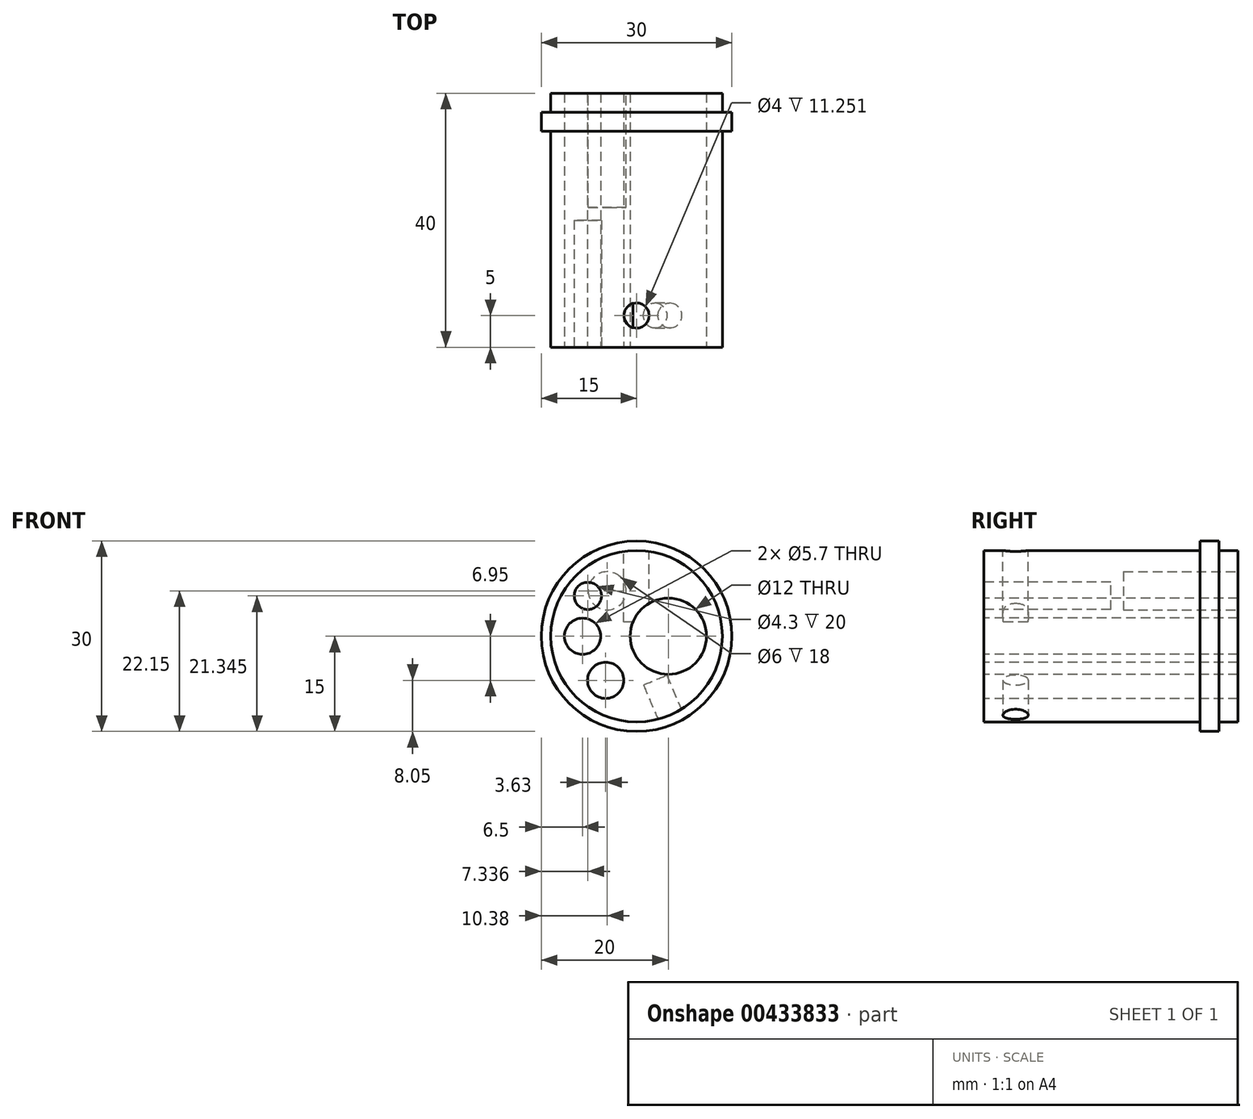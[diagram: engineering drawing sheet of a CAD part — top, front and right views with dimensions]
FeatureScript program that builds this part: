
annotation { "Feature Type Name" : "Feature", "Feature Type Description" : "" }
export const myFeature = defineFeature(function(context is Context, id is Id, definition is map)
    precondition{}
    {
        {
            var Q0;
            Q0=qCreatedBy(makeId("Front.planeOp"),FACE);
            var sketch = newSketch(context, id + "F0", { "sketchPlane" : qUnion([Q0])});
            skCircle(sketch, "E0", {"center": v(0, 0) * mm, "radius": 15 * mm});
            skSolve(sketch);
        }
        {
            var Q0;
            Q0 = qSketchRegion(id + "F0", true);
            extrude(context, id + "F1", {"entities" : qUnion([Q0]), "oppositeDirection" : true, "depth" : 40 * mm});
        }
        {
            var Q0;
            Q0=makeQuery(id+"F1.opExtrude","CAP_FACE",FACE,{"disambiguationData":[OSD([sQuery(id+"F0.wireOp",EDGE,"E0")])],"isStart":true});
            var sketch = newSketch(context, id + "F2", { "sketchPlane" : qUnion([Q0])});
            skCircle(sketch, "E1", {"center": v(0, 0) * mm, "radius": 25.45 * mm});
            skCircle(sketch, "E2", {"center": v(0, 0) * mm, "radius": 13.5 * mm});
            skSolve(sketch);
        }
        {
            var Q0;
            Q0 = qSketchRegion(id + "F2", true);
            extrude(context, id + "F3", {"entities" : qUnion([Q0]), "operationType" : NewBodyOperationType.REMOVE, "oppositeDirection" : true, "depth" : 34 * mm});
        }
        {
            var Q0;
            Q0=makeQuery(id+"F1.opExtrude","CAP_FACE",FACE,{"disambiguationData":[OSD([sQuery(id+"F0.wireOp",EDGE,"E0")])],"isStart":false});
            var sketch = newSketch(context, id + "F4", { "sketchPlane" : qUnion([Q0])});
            skCircle(sketch, "E3", {"center": v(0, 0) * mm, "radius": 18.73 * mm});
            skCircle(sketch, "E4", {"center": v(0, 0) * mm, "radius": 13.5 * mm});
            skSolve(sketch);
        }
        {
            var Q0;
            Q0 = qSketchRegion(id + "F4", true);
            extrude(context, id + "F5", {"entities" : qUnion([Q0]), "operationType" : NewBodyOperationType.REMOVE, "oppositeDirection" : true, "depth" : 3 * mm});
        }
        {
            var Q0;
            Q0=makeQuery(id+"F1.opExtrude","CAP_FACE",FACE,{"disambiguationData":[OSD([sQuery(id+"F0.wireOp",EDGE,"E0")])],"isStart":true});
            var sketch = newSketch(context, id + "F6", { "sketchPlane" : qUnion([Q0])});
            skCircle(sketch, "E5", {"center": v(5, 0) * mm, "radius": 6 * mm});
            skSolve(sketch);
        }
        {
            var Q0;
            Q0 = qSketchRegion(id + "F6", true);
            extrude(context, id + "F7", {"entities" : qUnion([Q0]), "operationType" : NewBodyOperationType.REMOVE, "endBound" : BoundingType.THROUGH_ALL, "oppositeDirection" : true, "depth" : 25 * mm});
        }
        {
            var Q0;
            Q0=makeQuery(id+"F1.opExtrude","CAP_FACE",FACE,{"disambiguationData":[OSD([sQuery(id+"F0.wireOp",EDGE,"E0")])],"isStart":true});
            var sketch = newSketch(context, id + "F8", { "sketchPlane" : qUnion([Q0])});
            skCircle(sketch, "E6", {"center": v(-4.87, -6.95) * mm, "radius": 2.85 * mm});
            skSolve(sketch);
        }
        {
            var Q0;
            Q0 = qSketchRegion(id + "F8", true);
            extrude(context, id + "F9", {"entities" : qUnion([Q0]), "operationType" : NewBodyOperationType.REMOVE, "endBound" : BoundingType.THROUGH_ALL, "oppositeDirection" : true, "depth" : 25 * mm});
        }
        {
            var Q0;
            Q0=makeQuery(id+"F1.opExtrude","CAP_FACE",FACE,{"disambiguationData":[OSD([sQuery(id+"F0.wireOp",EDGE,"E0")])],"isStart":true});
            var sketch = newSketch(context, id + "F10", { "sketchPlane" : qUnion([Q0])});
            skCircle(sketch, "E7", {"center": v(-8.5, 0) * mm, "radius": 2.85 * mm});
            skPoint(sketch, "E8", {"position": v(-4.87, -6.95) * mm});
            skSolve(sketch);
        }
        {
            var Q0;
            Q0 = qSketchRegion(id + "F10", true);
            extrude(context, id + "F11", {"entities" : qUnion([Q0]), "operationType" : NewBodyOperationType.REMOVE, "endBound" : BoundingType.THROUGH_ALL, "oppositeDirection" : true, "depth" : 25 * mm});
        }
        {
            var Q0;
            Q0=makeQuery(id+"F1.opExtrude","CAP_FACE",FACE,{"disambiguationData":[OSD([sQuery(id+"F0.wireOp",EDGE,"E0")])],"isStart":true});
            var sketch = newSketch(context, id + "F12", { "sketchPlane" : qUnion([Q0])});
            skCircle(sketch, "E9", {"center": v(-7.66, 6.35) * mm, "radius": 2.15 * mm});
            skSolve(sketch);
        }
        {
            var Q0;
            Q0 = qSketchRegion(id + "F12", true);
            extrude(context, id + "F13", {"entities" : qUnion([Q0]), "operationType" : NewBodyOperationType.REMOVE, "oppositeDirection" : true, "depth" : 20 * mm});
        }
        {
            var Q0;
            Q0=makeQuery(id+"F1.opExtrude","CAP_FACE",FACE,{"disambiguationData":[OSD([sQuery(id+"F0.wireOp",EDGE,"E0")])],"isStart":false});
            var sketch = newSketch(context, id + "F14", { "sketchPlane" : qUnion([Q0])});
            skCircle(sketch, "E10", {"center": v(4.62, 7.15) * mm, "radius": 3 * mm});
            skPoint(sketch, "E11", {"position": v(8.5, 0) * mm});
            skPoint(sketch, "E12", {"position": v(4.87, -6.95) * mm});
            skSolve(sketch);
        }
        {
            var Q0;
            Q0 = qSketchRegion(id + "F14", true);
            extrude(context, id + "F15", {"entities" : qUnion([Q0]), "operationType" : NewBodyOperationType.REMOVE, "oppositeDirection" : true, "depth" : 18 * mm});
        }
        {
            var Q0;
            Q0=qCreatedBy(makeId("Top.planeOp"),FACE);
            cPlane(context, id + "F16", {"entities" : qUnion([Q0]), "cplaneType" : CPlaneType.OFFSET, "offset" : 13.75 * mm, "width" : 150 * mm, "height" : 150 * mm});
        }
        {
            var Q0;
            Q0=qCreatedBy(id+"F16.planeOp",FACE);
            var sketch = newSketch(context, id + "F17", { "sketchPlane" : qUnion([Q0])});
            skCircle(sketch, "E13", {"center": v(0, 5) * mm, "radius": 2 * mm});
            skSolve(sketch);
        }
        {
            var Q0;
            Q0 = qSketchRegion(id + "F17", true);
            extrude(context, id + "F18", {"entities" : qUnion([Q0]), "operationType" : NewBodyOperationType.REMOVE, "oppositeDirection" : true, "depth" : 11.5 * mm});
        }
        {
            var Q0;
            Q0=makeQuery(id+"F3.boolean.opBoolean","COPY",FACE,{"derivedFrom":makeQuery(id+"F3.opExtrude","CAP_FACE",FACE,{"disambiguationData":[OSD([sQuery(id+"F2.wireOp",EDGE,"E1"),sQuery(id+"F2.wireOp",EDGE,"E2")])],"isStart":false})});
            cPlane(context, id + "F19", {"entities" : qUnion([Q0]), "cplaneType" : CPlaneType.OFFSET, "offset" : 29 * mm, "width" : 150 * mm, "height" : 150 * mm});
        }
        {
            var Q0;
            Q0=qCreatedBy(id+"F19.planeOp",FACE);
            var sketch = newSketch(context, id + "F20", { "sketchPlane" : qUnion([Q0])});
            skLineSegment(sketch, "E14", {"start": v(0, 0) * mm, "end": v(5.27, -12.43) * mm, "construction": true});
            skLineSegment(sketch, "E15", {"start": v(0, 0) * mm, "end": v(0, -21.01) * mm, "construction": true});
            skLineSegment(sketch, "E16", {"start": v(2.93, -6.9) * mm, "end": v(5.27, -12.43) * mm});
            skLineSegment(sketch, "E17", {"start": v(5.27, -12.43) * mm, "end": v(3.43, -13.2) * mm});
            skLineSegment(sketch, "E18", {"start": v(3.43, -13.2) * mm, "end": v(1.09, -7.69) * mm});
            skLineSegment(sketch, "E19", {"start": v(1.09, -7.69) * mm, "end": v(2.93, -6.9) * mm});
            skSolve(sketch);
        }
        {
            var Q0;
            Q0 = qSketchRegion(id + "F20", true);
            var Q1;
            Q1=sQuery(id+"F20.wireOp",EDGE,"E14");
            revolve(context, id + "F21", {"operationType" : NewBodyOperationType.REMOVE, "entities" : qUnion([Q0]), "axis" : qUnion([Q1]), "revolveType" : RevolveType.FULL, "oppositeDirection" : true});
        }
    });
